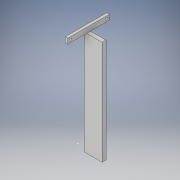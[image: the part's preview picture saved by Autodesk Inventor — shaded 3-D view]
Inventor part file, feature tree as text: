
AUTODESK INVENTOR PART (.ipt)
format: ipt  version: 2017 (Build 210142000, 142)  size: 165,888 bytes
history: native  units: in
note: dims shown in document units (in); Inventor stores cm internally (conversion verified against a paired STEP export)
features: sketch x6, extrude x3, hole x2, projected_geometry x2
ambient origin geometry x8: Origin, YZ Plane, XZ Plane, XY Plane, X Axis, Y Axis, Z Axis, Center Point
bodies: Solid1 (feature_tree)
feature tree (13):
  extrude  "Extrusion1"  Depth=10.0in
  extrude  "Extrusion4"  Depth=0.375in
  sketch  "Sketch5"  dims[d12=5.0in d13=0.0in]
  hole  "Hole2"  [1 undecoded]
  extrude  "Extrusion7"  Depth=0.375in
  hole  "Hole3"  [1 undecoded]
  sketch  "Sketch1"  dims[d0=2.725in d1=10.0in]
  sketch  "Sketch4"  dims[d2=0.375in d3=0.0in d11=0.975in]
  sketch  "Sketch9"  dims[d34=0.13in d35=0.25in d36=0.375in d37=0.25in d38=0.5635in d39=0.3in d40=0.8108in d41=0.25in]
  sketch  "Sketch11"  dims[d42=4.0in d44=0.375in]
  projected_geometry  "Projected Loop1"
  sketch  "Sketch12"  dims[d45=1.8125in d46=0.0in d47=0.5in d48=0.0in d49=0.5in d50=0.25in d51=0.25in d52=0.25in d53=0.25in d54=0.25in d55=0.75in d56=0.375in d57=0.25in d58=0.5635in d59=1.0in d60=0.8108in]
  projected_geometry  "Projected Loop2"
note: 2 required parameter values undecoded (feature->parameter linkage not recoverable at this tier; creation-order binding heuristic only, values carry confidence <= 0.55)
